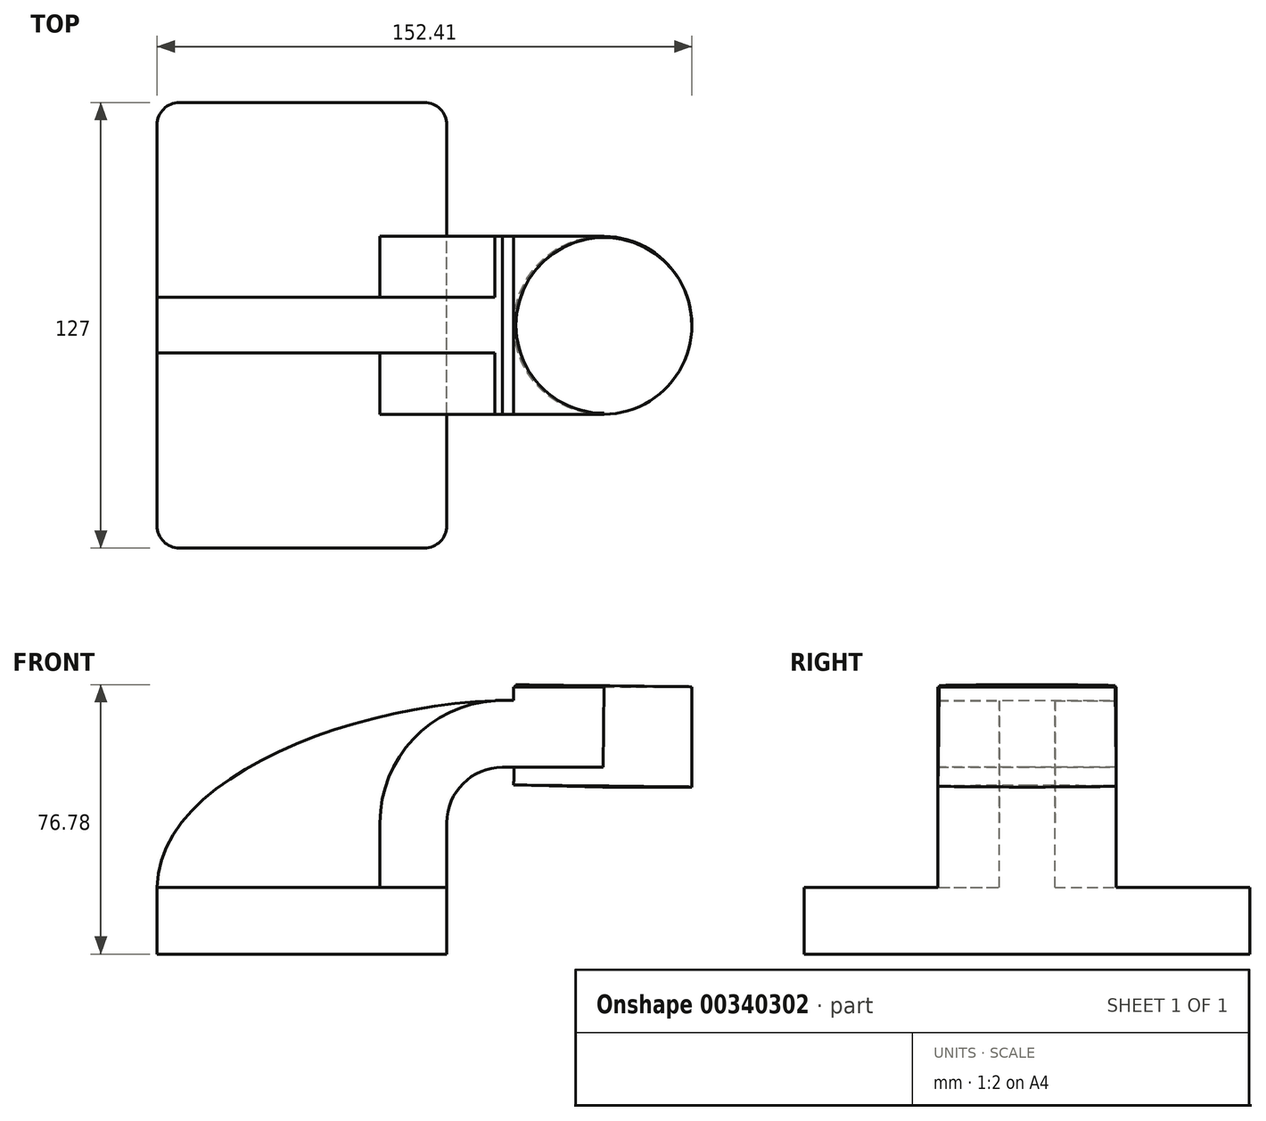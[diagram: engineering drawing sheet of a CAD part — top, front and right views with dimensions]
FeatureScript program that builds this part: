
annotation { "Feature Type Name" : "Feature", "Feature Type Description" : "" }
export const myFeature = defineFeature(function(context is Context, id is Id, definition is map)
    precondition{}
    {
        {
            var Q0;
            Q0=qCreatedBy(makeId("Front.planeOp"),FACE);
            var sketch = newSketch(context, id + "F0", { "sketchPlane" : qUnion([Q0])});
            skLineSegment(sketch, "E0.bottom", {"start": v(-41.28, 9.52) * mm, "end": v(41.27, 9.53) * mm});
            skLineSegment(sketch, "E0.top", {"start": v(-41.28, -9.53) * mm, "end": v(41.28, -9.53) * mm});
            skLineSegment(sketch, "E0.left", {"start": v(-41.28, 9.52) * mm, "end": v(-41.27, -9.53) * mm});
            skLineSegment(sketch, "E0.right", {"start": v(41.28, 9.53) * mm, "end": v(41.28, -9.52) * mm});
            skPoint(sketch, "E0.middle", {"position": v(0, 0) * mm});
            skLineSegment(sketch, "E1.bottom", {"start": v(111.13, 38.1) * mm, "end": v(60.33, 38.1) * mm});
            skLineSegment(sketch, "E1.top", {"start": v(111.13, 66.68) * mm, "end": v(60.32, 66.68) * mm});
            skLineSegment(sketch, "E1.left", {"start": v(111.13, 38.1) * mm, "end": v(111.13, 66.68) * mm});
            skLineSegment(sketch, "E1.right", {"start": v(60.33, 38.1) * mm, "end": v(60.32, 66.68) * mm});
            skPoint(sketch, "E1.middle", {"position": v(85.73, 52.39) * mm});
            skLineSegment(sketch, "E2", {"start": v(41.27, 9.53) * mm, "end": v(41.27, 27.88) * mm});
            skArc(sketch, "E3", {"start": v(41.27, 27.88) * mm, "mid": v(45.92, 39.1) * mm, "end": v(57.15, 43.76) * mm});
            skLineSegment(sketch, "E4.0", {"start": v(57.15, 62.8) * mm, "end": v(85.72, 62.8) * mm});
            skArc(sketch, "E4.1", {"start": v(22.23, 27.88) * mm, "mid": v(32.45, 52.58) * mm, "end": v(57.15, 62.8) * mm});
            skLineSegment(sketch, "E4.2", {"start": v(22.22, 9.53) * mm, "end": v(22.22, 27.88) * mm});
            skLineSegment(sketch, "E5", {"start": v(57.15, 43.76) * mm, "end": v(86.05, 43.76) * mm});
            skLineSegment(sketch, "E6", {"start": v(85.72, 38.1) * mm, "end": v(86.05, 66.68) * mm});
            skFitSpline(sketch, "E7", {"points": [v(-41.28, 9.53) * mm, v(57.15, 62.8) * mm], "startDerivative": vector(0.63, 92.93) * mm, "endDerivative": vector(130.14, 3.06) * mm});
            skSolve(sketch);
        }
        {
            var Q0;
            Q0=makeQuery(id+"F0.imprint","IMPRINT",FACE,{"disambiguationData":[TD([[makeQuery(id+"F0.imprint","IMPRINT",EDGE,{"derivedFrom":sQuery(id+"F0.wireOp",EDGE,"E0.top")}),1.0]])]});
            extrude(context, id + "F1", {"entities" : qUnion([Q0]), "endBound" : BoundingType.SYMMETRIC, "depth" : 127 * mm});
        }
        {
            var Q0;
            {var subQ1=sQuery(id+"F0.wireOp",EDGE,"E2");Q0=makeQuery(id+"F0.imprint","IMPRINT",FACE,{"disambiguationData":[TD([[makeQuery(id+"F0.imprint","IMPRINT",EDGE,{"derivedFrom":subQ1}),1.0]])]});}
            var Q1;
            {var subQ1=sQuery(id+"F0.wireOp",EDGE,"E1.right");var subQ5=sQuery(id+"F0.wireOp",EDGE,"E1.top");var subQ6=makeQuery(id+"F0.imprint","INTERSECT",VERTEX,{"derivedFrom":[subQ5,subQ1]});Q1=makeQuery(id+"F0.imprint","IMPRINT",FACE,{"disambiguationData":[TD([[makeQuery(id+"F0.imprint","IMPRINT",EDGE,{"disambiguationData":[TD([[subQ6,1.0]])],"derivedFrom":subQ5}),1.0]])]});}
            extrude(context, id + "F2", {"entities" : qUnion([Q0, Q1]), "operationType" : NewBodyOperationType.ADD, "endBound" : BoundingType.SYMMETRIC, "depth" : 50.8 * mm});
        }
        {
            var Q0;
            {var subQ3=sQuery(id+"F0.wireOp",EDGE,"E4.2");Q0=makeQuery(id+"F0.imprint","IMPRINT",FACE,{"disambiguationData":[TD([[makeQuery(id+"F0.imprint","IMPRINT",EDGE,{"derivedFrom":subQ3}),1.0]])]});}
            extrude(context, id + "F3", {"entities" : qUnion([Q0]), "operationType" : NewBodyOperationType.ADD, "endBound" : BoundingType.SYMMETRIC, "depth" : 15.88 * mm});
        }
        {
            var Q0;
            {var subQ4=sQuery(id+"F0.wireOp",EDGE,"E1.left");Q0=makeQuery(id+"F0.imprint","IMPRINT",FACE,{"disambiguationData":[TD([[makeQuery(id+"F0.imprint","IMPRINT",EDGE,{"derivedFrom":subQ4}),1.0]])]});}
            var Q1;
            Q1=sQuery(id+"F0.wireOp",EDGE,"E6");
            revolve(context, id + "F4", {"operationType" : NewBodyOperationType.ADD, "entities" : qUnion([Q0]), "axis" : qUnion([Q1]), "revolveType" : RevolveType.FULL});
        }
        {
            var Q0;
            Q0=makeQuery(id+"F1.opExtrude","CAP_EDGE",EDGE,{"disambiguationData":[OSD([sQuery(id+"F0.wireOp",EDGE,"E0.right")])],"isStart":false});
            var Q1;
            Q1=makeQuery(id+"F1.opExtrude","CAP_EDGE",EDGE,{"disambiguationData":[OSD([sQuery(id+"F0.wireOp",EDGE,"E0.left")])],"isStart":false});
            var Q2;
            Q2=makeQuery(id+"F1.opExtrude","CAP_EDGE",EDGE,{"disambiguationData":[OSD([sQuery(id+"F0.wireOp",EDGE,"E0.left")])],"isStart":true});
            var Q3;
            Q3=makeQuery(id+"F1.opExtrude","CAP_EDGE",EDGE,{"disambiguationData":[OSD([sQuery(id+"F0.wireOp",EDGE,"E0.right")])],"isStart":true});
            fillet(context, id + "F5", {"entities" : qUnion([Q0, Q1, Q2, Q3]), "radius" : 6.35 * mm, "tangentPropagation" : true, "allowEdgeOverflow" : false});
        }
    });
